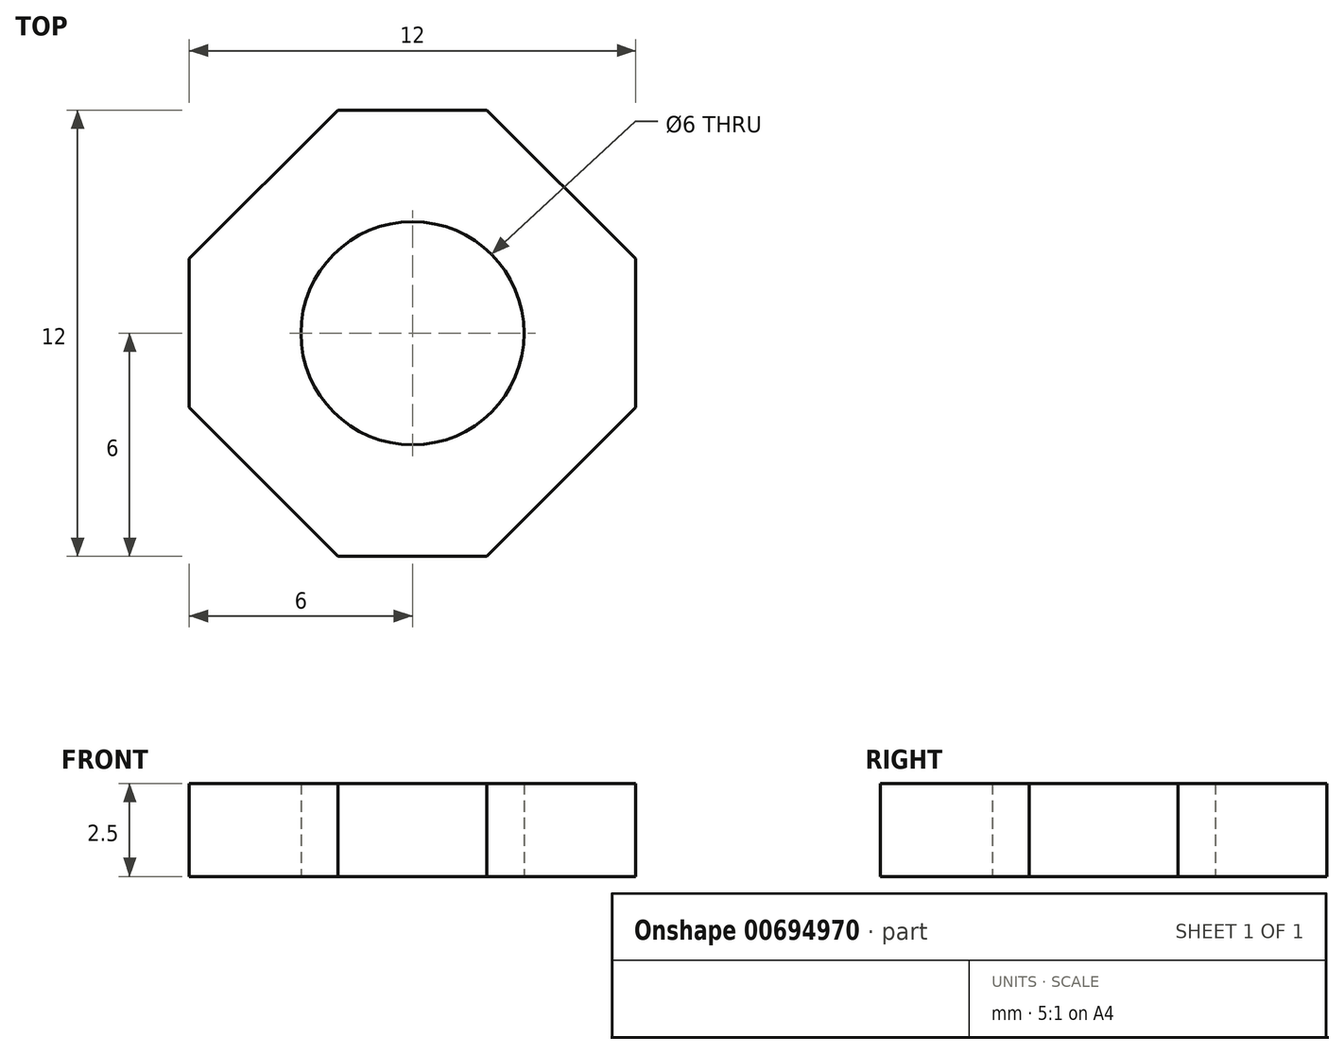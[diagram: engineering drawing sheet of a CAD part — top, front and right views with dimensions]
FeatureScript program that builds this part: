
annotation { "Feature Type Name" : "Feature", "Feature Type Description" : "" }
export const myFeature = defineFeature(function(context is Context, id is Id, definition is map)
    precondition{}
    {
        {
            var Q0;
            Q0=qCreatedBy(makeId("Top.planeOp"),FACE);
            var sketch = newSketch(context, id + "F0", { "sketchPlane" : qUnion([Q0])});
            skCircle(sketch, "E0", {"center": v(2.22, 0) * mm, "radius": 3 * mm});
            skLineSegment(sketch, "E1", {"start": v(-3.96, 78) * mm, "end": v(8.62, 78) * mm});
            skLineSegment(sketch, "E2.bottom", {"start": v(-3.78, 6) * mm, "end": v(8.22, 6) * mm});
            skLineSegment(sketch, "E2.top", {"start": v(-3.78, -6) * mm, "end": v(8.22, -6) * mm});
            skLineSegment(sketch, "E2.left", {"start": v(-3.78, 6) * mm, "end": v(-3.78, -6) * mm});
            skLineSegment(sketch, "E2.right", {"start": v(8.22, 6) * mm, "end": v(8.22, -6) * mm});
            skLineSegment(sketch, "E3.bottom", {"start": v(0, 6) * mm, "end": v(5, 6) * mm});
            skLineSegment(sketch, "E3.top", {"start": v(0, 84) * mm, "end": v(5, 84) * mm});
            skLineSegment(sketch, "E3.left", {"start": v(0, 6) * mm, "end": v(0, 84) * mm});
            skLineSegment(sketch, "E3.right", {"start": v(5, 6) * mm, "end": v(5, 84) * mm});
            skSolve(sketch);
        }
        {
            var Q0;
            Q0=makeQuery(id+"F0.imprint","IMPRINT",FACE,{"disambiguationData":[TD([[makeQuery(id+"F0.imprint","IMPRINT",EDGE,{"derivedFrom":sQuery(id+"F0.wireOp",EDGE,"E0")}),-1.0]])]});
            var Q1;
            {var subQ5=sQuery(id+"F0.wireOp",EDGE,"E3.bottom");Q1=makeQuery(id+"F0.imprint","IMPRINT",FACE,{"disambiguationData":[TD([[makeQuery(id+"F0.imprint","IMPRINT",EDGE,{"derivedFrom":subQ5}),1.0]])]});}
            extrude(context, id + "F1", {"entities" : qUnion([Q0, Q1]), "depth" : 2.5 * mm, "offsetDistance" : 25 * mm});
        }
        {
            var Q0;
            Q0=makeQuery(id+"F1.opExtrude","SWEPT_EDGE",EDGE,{"disambiguationData":[OSD([sQuery(id+"F0.wireOp",EDGE,"E2.top"),sQuery(id+"F0.wireOp",EDGE,"E2.right")])]});
            var Q1;
            Q1=makeQuery(id+"F1.opExtrude","SWEPT_EDGE",EDGE,{"disambiguationData":[OSD([sQuery(id+"F0.wireOp",EDGE,"E2.top"),sQuery(id+"F0.wireOp",EDGE,"E2.left")])]});
            var Q2;
            Q2=makeQuery(id+"F1.opExtrude","SWEPT_EDGE",EDGE,{"disambiguationData":[OSD([sQuery(id+"F0.wireOp",EDGE,"E2.bottom"),sQuery(id+"F0.wireOp",EDGE,"E2.left")])]});
            var Q3;
            Q3=makeQuery(id+"F1.opExtrude","SWEPT_EDGE",EDGE,{"disambiguationData":[OSD([sQuery(id+"F0.wireOp",EDGE,"E2.bottom"),sQuery(id+"F0.wireOp",EDGE,"E2.right")])]});
            chamfer(context, id + "F2", {"entities" : qUnion([Q0, Q1, Q2, Q3]), "width" : 4 * mm, "tangentPropagation" : true});
        }
    });
